# Revit family: Haworth_Fern_Chair_Task_Executive_AP_PRELIMINARY
name_source: partatom
category: Furniture
revit_build: Autodesk Revit 2018 (Build: 20170223_1515(x64)
units: mm (PartAtom-declared; Revit-internal decimal feet)

## family parameters
Always vertical = Yes
Cut with Voids When Loaded = No
OmniClass Number = 23.40.20.00
OmniClass Title = General Furniture and Specialties
Room Calculation Point = No
Shared = No
Work Plane-Based = No

## types (4) — shared parameters
Assembly Code = E2020200
Caster Finish = Haworth _ Polymer _ Fog
Depth = 610 mm
Description = Haworth - Fern - Chair - Task - Executive
Hardware Finish = Haworth _ Polymer _ Black
Height = 1118 mm
Manufacturer = Haworth
Model = SEFNEMX
Post Finish = Haworth _ Metal _ Polished Aluminum
Size = Verify Final Dim. w/Haworth
URL = https://www.haworth.com
URL - Product = https://www.haworth.com
Version = 4
Warranty = http://www.haworth.com
Width = 711 mm

## per-type parameters (varying)
| type | 4D Arms | Ht Adj Arms Actual |
| 4D Arms | Yes | Yes |
| Height Adjustable Arms | No | Yes |
| Fixed Arms | No | No |
| Without Arms | No | No |

type visibility flags (boolean, named after types; folded from table):
- 4D Arms: Yes: (none)
- Height Adjustable Arms: Yes: Height Adjustable Arms
- Fixed Arms: Yes: Fixed Arms
- Without Arms: Yes: Without Arms

## geometry (parser evidence)
native form markers: Sweep x12
no freeform markers — native parametric forms only
